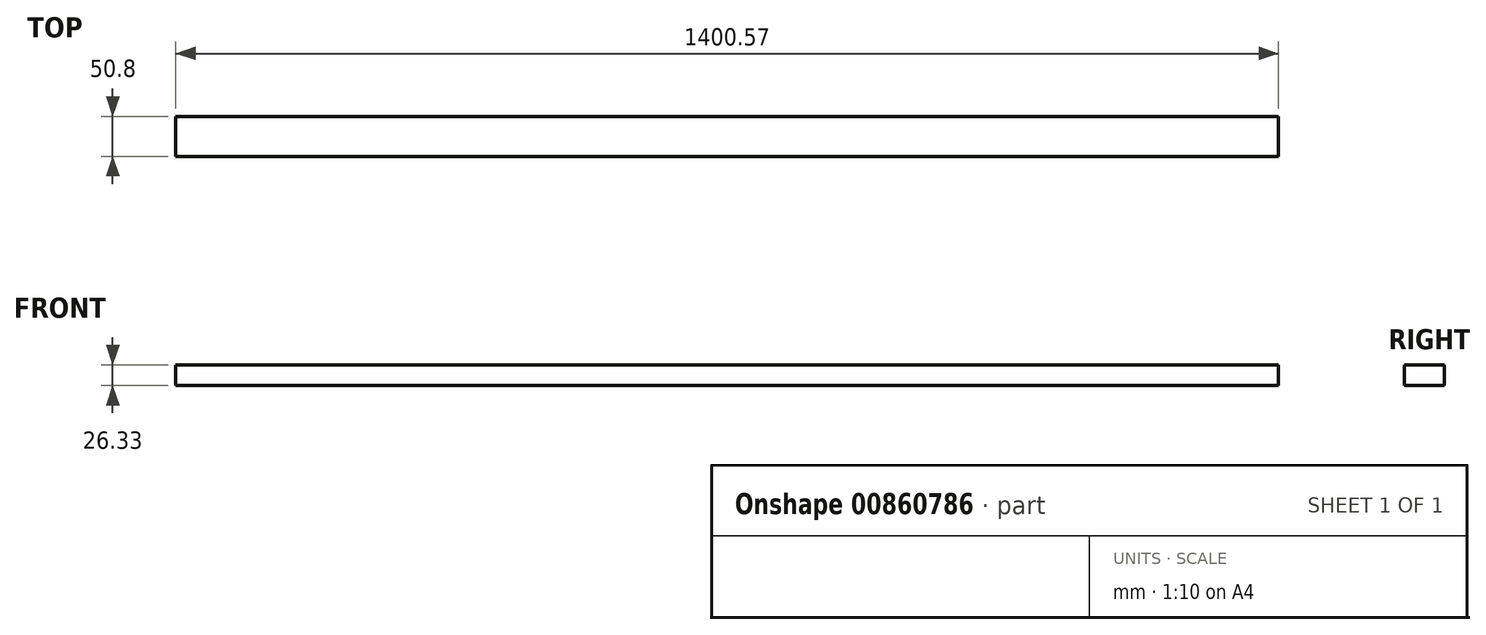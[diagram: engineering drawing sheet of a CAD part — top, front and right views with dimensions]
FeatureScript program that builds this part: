
annotation { "Feature Type Name" : "Feature", "Feature Type Description" : "" }
export const myFeature = defineFeature(function(context is Context, id is Id, definition is map)
    precondition{}
    {
        {
            var Q0;
            Q0=qCreatedBy(makeId("Front.planeOp"),FACE);
            var sketch = newSketch(context, id + "F0", { "sketchPlane" : qUnion([Q0])});
            skLineSegment(sketch, "E0", {"start": v(0, 0) * mm, "end": v(1400.57, 0) * mm});
            skLineSegment(sketch, "E1", {"start": v(1400.57, 0) * mm, "end": v(1400.57, 26.33) * mm});
            skLineSegment(sketch, "E2", {"start": v(1400.57, 26.33) * mm, "end": v(0, 26.33) * mm});
            skLineSegment(sketch, "E3", {"start": v(0, 26.33) * mm, "end": v(0, 0) * mm});
            skSolve(sketch);
        }
        {
            var Q0;
            Q0 = qSketchRegion(id + "F0", true);
            extrude(context, id + "F1", {"entities" : qUnion([Q0]), "depth" : 50.8 * mm, "offsetDistance" : 25.4 * mm});
        }
    });
